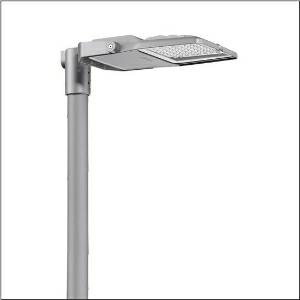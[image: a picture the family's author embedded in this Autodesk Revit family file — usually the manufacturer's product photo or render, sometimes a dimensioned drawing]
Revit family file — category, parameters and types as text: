
# Revit family: floodlight_fl_21_iq_mini___pl64_5xa7771c4e3a_84b6
name_source: partatom
category: Lighting Fixtures
units: mm (PartAtom-declared; Revit-internal decimal feet)

## family parameters
Cut with Voids When Loaded = No
Host = Face
Light Source = No
Part Type = Normal
Room Calculation Point = No
Round Connector Dimension = Use Diameter
Shared = No

## types (1)
- --- (1 x LED, 12280 lm, 87.2 W, 4000K)
    Apparent Load = 87 VA
    CIE Flux Codes = 28 80 98 100 100
    Color Rendering = 70
    Color Temperature = 4000K
    Default Elevation = 1800 mm
    Description = Floodlight FL 21 iQ mini, floodlight, primary light control with lens, of PMMA, primary optical cover: protective disc, of toughened safety glass, transparent, light distribution: PL64, light emission: direct distribution, installation type: surface-mounted, LED, High Power LED, rated luminous flux: 12.280lm, luminous efficacy: 141lm/W, light colour: 740, colour temperature: 4000K, control gear: iQ Comfort/DALI, control: Auto-Match, Temp-Guard, Lumen-Switch, Night-Set, Smart-Wire, Light-Fading, Desk-Remote (wireless, voltage-free reading and setting of iQ features in the workshop via application-optimized NFC function/RFID function), optimised constant luminous flux control (CLO 2.0), with terminal, 6-pole, mains connection: 220..240V, AC, 50/60Hz, start of lifetime: 87W, end of service life: 92W, reduction: 40W, luminaire housing, of diecast aluminium, powder-coated, Siteco® metallic grey (DB 702S), corrosivity category C5 mid according to DIN EN ISO 12944, suitable for swimming pools, chlorine-resistant, sealing non-destructively replaceable, please order mast flange separately, mast bracket, of steel, galvanised, powder-coated, Siteco® metallic grey (DB 702S), protection rating (complete): IP66, insulation class (complete): insulation class II (safety insulation), certification: CE, ENEC, VDE, protection symbol: D, impact resistance: IK08, permissible operating ambient temperature: -40..+40°C, permissible operating ambient temperature for outdoor applications: -40..+50°C, standard: DIN EN 12944, LABS conformity tested according to VDMA 24364:2018-05, packaging unit: 1 piece

Light Distribution: PL64
    Height = 70 mm
    Lamp = 1 x LED
    Lamp Light Flux = 12280 lm
    Lamp Power = 87.2 W
    Lamp count = 1
    Length = 485 mm
    Luminous efficacy = 141 lm/W
    Manufacturer = Siteco
    ModVariant = No
    Model = 5XA7771C4E3A
    Number of Poles = 1
    OnlyDefault = Yes
    Power Factor = 1
    Product Name = Floodlight FL 21 iQ mini | PL64
    Product group = floodlight | pylon annexe
    ProductGroupID = 6200
    Protection Class = Protection class II
    Protection Degree = IP 66
    RLX_Detail_Level = 1
    RLX_Emergency_Light_Flux = 0 lm
    RLX_Emergency_Type = 0
    RLX_Emergency_Type_DB = No
    RlxData = <blob elided: 101349 chars, md5=65268041>
    Socket = socket
    Standby Power = 0 W
    System Light Flux = 12280 lm
    System Power = 87 W
    Type Comments = factory setting: luminous flux: 100 % | dim-lin: 254 | 456 mA
    Type Image = l_1007125.jpg
    URL = http://relux.com
    VarID = @adj_166506
    Voltage = 0 V
    Weight = 0.00 kg
    Width = 337 mm

## geometry (parser evidence)
native form markers: Blend x4, Sweep x12
no freeform markers — native parametric forms only
